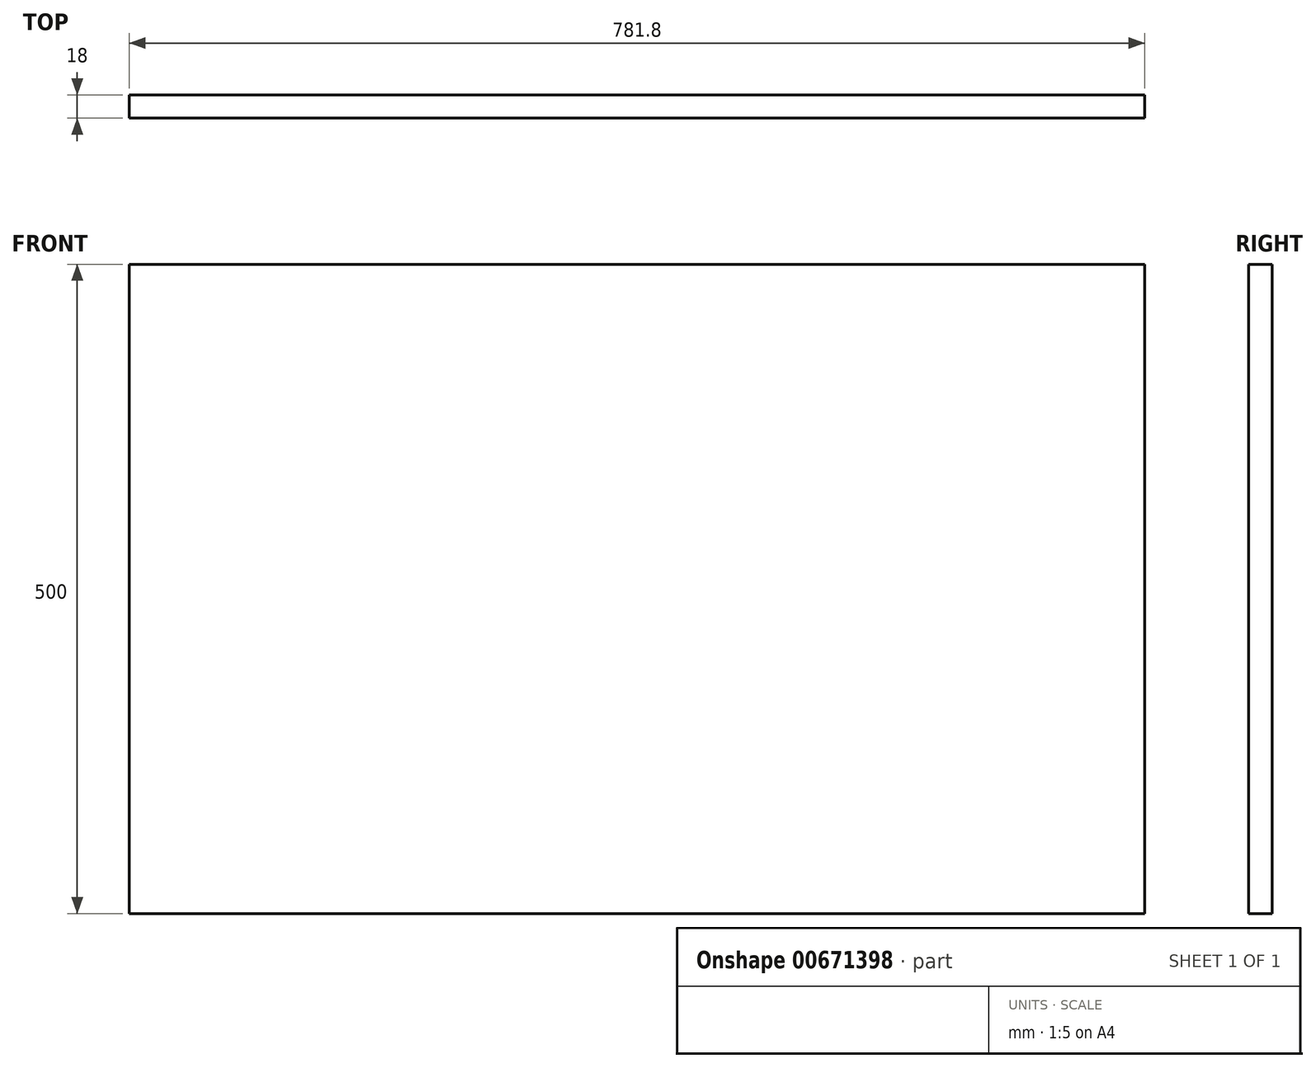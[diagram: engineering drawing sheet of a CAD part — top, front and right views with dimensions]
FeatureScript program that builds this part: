
annotation { "Feature Type Name" : "Feature", "Feature Type Description" : "" }
export const myFeature = defineFeature(function(context is Context, id is Id, definition is map)
    precondition{}
    {
        {
            var Q0;
            Q0=qCreatedBy(makeId("Front.planeOp"),FACE);
            var sketch = newSketch(context, id + "F0", { "sketchPlane" : qUnion([Q0])});
            skLineSegment(sketch, "E0.bottom", {"start": v(460.53, -233.48) * mm, "end": v(-321.27, -233.48) * mm});
            skLineSegment(sketch, "E0.top", {"start": v(460.53, 266.52) * mm, "end": v(-321.27, 266.52) * mm});
            skLineSegment(sketch, "E0.left", {"start": v(460.53, -233.48) * mm, "end": v(460.53, 266.52) * mm});
            skLineSegment(sketch, "E0.right", {"start": v(-321.27, -233.48) * mm, "end": v(-321.27, 266.52) * mm});
            skPoint(sketch, "E0.middle", {"position": v(69.63, 16.52) * mm});
            skSolve(sketch);
        }
        {
            var Q0;
            Q0=makeQuery(id+"F0.imprint","IMPRINT",FACE,{"disambiguationData":[TD([[makeQuery(id+"F0.imprint","IMPRINT",EDGE,{"derivedFrom":sQuery(id+"F0.wireOp",EDGE,"E0.bottom")}),-1.0]])]});
            extrude(context, id + "F1", {"entities" : qUnion([Q0]), "endBound" : BoundingType.SYMMETRIC, "depth" : 18 * mm, "offsetDistance" : 25 * mm});
        }
    });
